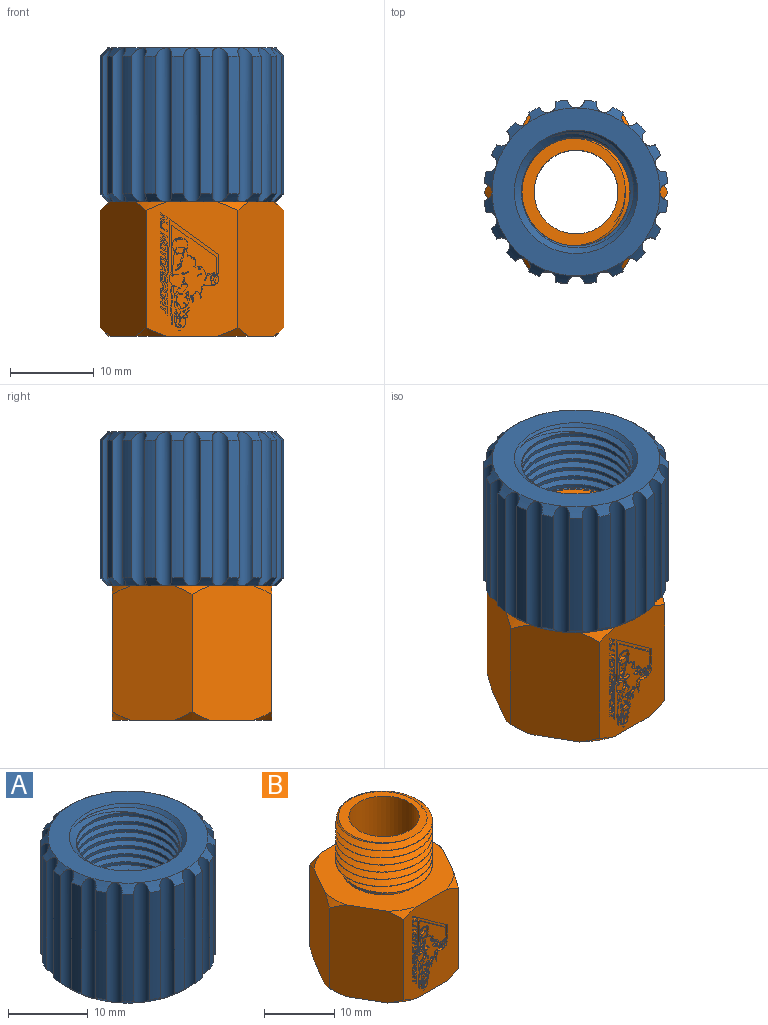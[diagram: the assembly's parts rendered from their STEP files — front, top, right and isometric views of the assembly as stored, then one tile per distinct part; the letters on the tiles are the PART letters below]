
ASSEMBLY  parts=2 mates=1
PART A: 89 faces, bbox 22x22x19 mm
  f0: cylinder r=1mm len=18.38mm, axis (0,0,1), area 53mm2, adj f35,f39,f60,f61,f80,f81
  f1: cylinder r=1mm len=18.38mm, axis (0,0,1), area 53mm2, adj f38,f39,f42,f60,f62,f80
  f2: cylinder r=1mm len=18.38mm, axis (0,0,1), area 53mm2, adj f37,f38,f42,f43,f62,f63
  f3: cylinder r=1mm len=18.38mm, axis (0,0,1), area 53mm2, adj f36,f37,f43,f44,f63,f64
  f4: cylinder r=1mm len=18.38mm, axis (0,0,1), area 53mm2, adj f34,f35,f59,f61,f79,f81
  f5: cylinder r=1mm len=18.38mm, axis (0,0,1), area 53mm2, adj f33,f34,f58,f59,f78,f79
  f6: cylinder r=1mm len=18.38mm, axis (0,0,1), area 53mm2, adj f32,f33,f57,f58,f77,f78
  f7: cylinder r=1mm len=18.38mm, axis (0,0,1), area 53mm2, adj f31,f32,f56,f57,f76,f77
  f8: cylinder r=1mm len=18.38mm, axis (0,0,1), area 53mm2, adj f30,f31,f55,f56,f75,f76
  f9: cylinder r=1mm len=18.38mm, axis (0,0,1), area 53mm2, adj f29,f30,f54,f55,f74,f75
  f10: cylinder r=1mm len=18.38mm, axis (0,0,1), area 53mm2, adj f28,f29,f53,f54,f73,f74
  f11: cylinder r=1mm len=18.38mm, axis (0,0,1), area 53mm2, adj f27,f28,f52,f53,f72,f73
  f12: cylinder r=1mm len=18.38mm, axis (0,0,1), area 53mm2, adj f26,f27,f51,f52,f71,f72
  f13: cylinder r=1mm len=18.38mm, axis (0,0,1), area 53mm2, adj f25,f26,f50,f51,f70,f71
  f14: cylinder r=1mm len=18.38mm, axis (0,0,1), area 53mm2, adj f24,f25,f49,f50,f69,f70
  f15: cylinder r=1mm len=18.38mm, axis (0,0,1), area 53mm2, adj f23,f24,f48,f49,f68,f69
  f16: cylinder r=1mm len=18.38mm, axis (0,0,1), area 53mm2, adj f22,f23,f47,f48,f67,f68
  f17: cylinder r=1mm len=18.38mm, axis (0,0,1), area 53mm2, adj f21,f22,f46,f47,f66,f67
  f18: cylinder r=1mm len=18.38mm, axis (0,0,1), area 53mm2, adj f20,f21,f45,f46,f65,f66
  f19: cylinder r=1mm len=18.38mm, axis (0,0,1), area 53mm2, adj f20,f36,f44,f45,f64,f65
  f20: cylinder r=11mm len=16.38mm, axis (0,0,-1), area 23.8mm2, adj f18,f19,f45,f65
  f21: cylinder r=11mm len=16.38mm, axis (0,0,-1), area 23.8mm2, adj f17,f18,f46,f66
  f22: cylinder r=11mm len=16.38mm, axis (0,0,-1), area 23.8mm2, adj f16,f17,f47,f67
  f23: cylinder r=11mm len=16.38mm, axis (0,0,-1), area 23.8mm2, adj f15,f16,f48,f68
  f24: cylinder r=11mm len=16.38mm, axis (0,0,-1), area 23.8mm2, adj f14,f15,f49,f69
  f25: cylinder r=11mm len=16.38mm, axis (0,0,-1), area 23.8mm2, adj f13,f14,f50,f70
  f26: cylinder r=11mm len=16.38mm, axis (0,0,-1), area 23.8mm2, adj f12,f13,f51,f71
  f27: cylinder r=11mm len=16.38mm, axis (0,0,-1), area 23.8mm2, adj f11,f12,f52,f72
  f28: cylinder r=11mm len=16.38mm, axis (0,0,-1), area 23.8mm2, adj f10,f11,f53,f73
  f29: cylinder r=11mm len=16.38mm, axis (0,0,-1), area 23.8mm2, adj f9,f10,f54,f74
  f30: cylinder r=11mm len=16.38mm, axis (0,0,-1), area 23.8mm2, adj f8,f9,f55,f75
  f31: cylinder r=11mm len=16.38mm, axis (0,0,-1), area 23.8mm2, adj f7,f8,f56,f76
  f32: cylinder r=11mm len=16.38mm, axis (0,0,-1), area 23.8mm2, adj f6,f7,f57,f77
  f33: cylinder r=11mm len=16.38mm, axis (0,0,-1), area 23.8mm2, adj f5,f6,f58,f78
  f34: cylinder r=11mm len=16.38mm, axis (0,0,-1), area 23.8mm2, adj f4,f5,f59,f79
  f35: cylinder r=11mm len=16.38mm, axis (0,0,-1), area 23.8mm2, adj f0,f4,f61,f81
  f36: cylinder r=11mm len=16.38mm, axis (0,0,-1), area 23.8mm2, adj f3,f19,f44,f64
  f37: cylinder r=11mm len=16.38mm, axis (0,0,-1), area 23.8mm2, adj f2,f3,f43,f63
  f38: cylinder r=11mm len=16.38mm, axis (0,0,-1), area 23.8mm2, adj f1,f2,f42,f62
  f39: cylinder r=11mm len=16.38mm, axis (0,0,-1), area 23.8mm2, adj f0,f1,f60,f80
  f40: plane 20x20mm, normal (0,0,1), area 144mm2, adj f62,f63,f64,f65,f66,f67,f68,f69
  f41: plane 20x20mm, normal (0,0,-1), area 137.4mm2, adj f42,f43,f44,f45,f46,f47,f48,f49
  f42: cone r=11mm half-angle=45deg, axis (0,0,1), area 2.5mm2, adj f1,f2,f38,f41
  f43: cone r=11mm half-angle=45deg, axis (0,0,1), area 2.5mm2, adj f2,f3,f37,f41
  f44: cone r=11mm half-angle=45deg, axis (0,0,1), area 2.5mm2, adj f3,f19,f36,f41
  f45: cone r=11mm half-angle=45deg, axis (0,0,1), area 2.5mm2, adj f18,f19,f20,f41
  f46: cone r=11mm half-angle=45deg, axis (0,0,1), area 2.5mm2, adj f17,f18,f21,f41
  f47: cone r=11mm half-angle=45deg, axis (0,0,1), area 2.5mm2, adj f16,f17,f22,f41
  f48: cone r=11mm half-angle=45deg, axis (0,0,1), area 2.5mm2, adj f15,f16,f23,f41
  f49: cone r=11mm half-angle=45deg, axis (0,0,1), area 2.5mm2, adj f14,f15,f24,f41
  f50: cone r=11mm half-angle=45deg, axis (0,0,1), area 2.5mm2, adj f13,f14,f25,f41
  f51: cone r=11mm half-angle=45deg, axis (0,0,1), area 2.5mm2, adj f12,f13,f26,f41
  f52: cone r=11mm half-angle=45deg, axis (0,0,1), area 2.5mm2, adj f11,f12,f27,f41
  f53: cone r=11mm half-angle=45deg, axis (0,0,1), area 2.5mm2, adj f10,f11,f28,f41
  f54: cone r=11mm half-angle=45deg, axis (0,0,1), area 2.5mm2, adj f9,f10,f29,f41
  f55: cone r=11mm half-angle=45deg, axis (0,0,1), area 2.5mm2, adj f8,f9,f30,f41
  f56: cone r=11mm half-angle=45deg, axis (0,0,1), area 2.5mm2, adj f7,f8,f31,f41
  f57: cone r=11mm half-angle=45deg, axis (0,0,1), area 2.5mm2, adj f6,f7,f32,f41
  f58: cone r=11mm half-angle=45deg, axis (0,0,1), area 2.5mm2, adj f5,f6,f33,f41
  f59: cone r=11mm half-angle=45deg, axis (0,0,1), area 2.5mm2, adj f4,f5,f34,f41
  f60: cone r=11mm half-angle=45deg, axis (0,0,1), area 2.5mm2, adj f0,f1,f39,f41
  f61: cone r=11mm half-angle=45deg, axis (0,0,1), area 2.5mm2, adj f0,f4,f35,f41
  f62: cone r=10mm half-angle=45deg, axis (0,0,-1), area 2.5mm2, adj f1,f2,f38,f40
  f63: cone r=10mm half-angle=45deg, axis (0,0,-1), area 2.5mm2, adj f2,f3,f37,f40
  f64: cone r=10mm half-angle=45deg, axis (0,0,-1), area 2.5mm2, adj f3,f19,f36,f40
  f65: cone r=10mm half-angle=45deg, axis (0,0,-1), area 2.5mm2, adj f18,f19,f20,f40
  f66: cone r=10mm half-angle=45deg, axis (0,0,-1), area 2.5mm2, adj f17,f18,f21,f40
  f67: cone r=10mm half-angle=45deg, axis (0,0,-1), area 2.5mm2, adj f16,f17,f22,f40
  f68: cone r=10mm half-angle=45deg, axis (0,0,-1), area 2.5mm2, adj f15,f16,f23,f40
  f69: cone r=10mm half-angle=45deg, axis (0,0,-1), area 2.5mm2, adj f14,f15,f24,f40
  f70: cone r=10mm half-angle=45deg, axis (0,0,-1), area 2.5mm2, adj f13,f14,f25,f40
  f71: cone r=10mm half-angle=45deg, axis (0,0,-1), area 2.5mm2, adj f12,f13,f26,f40
  f72: cone r=10mm half-angle=45deg, axis (0,0,-1), area 2.5mm2, adj f11,f12,f27,f40
  f73: cone r=10mm half-angle=45deg, axis (0,0,-1), area 2.5mm2, adj f10,f11,f28,f40
  f74: cone r=10mm half-angle=45deg, axis (0,0,-1), area 2.5mm2, adj f9,f10,f29,f40
  f75: cone r=10mm half-angle=45deg, axis (0,0,-1), area 2.5mm2, adj f8,f9,f30,f40
  f76: cone r=10mm half-angle=45deg, axis (0,0,-1), area 2.5mm2, adj f7,f8,f31,f40
  f77: cone r=10mm half-angle=45deg, axis (0,0,-1), area 2.5mm2, adj f6,f7,f32,f40
  f78: cone r=10mm half-angle=45deg, axis (0,0,-1), area 2.5mm2, adj f5,f6,f33,f40
  f79: cone r=10mm half-angle=45deg, axis (0,0,-1), area 2.5mm2, adj f4,f5,f34,f40
  f80: cone r=10mm half-angle=45deg, axis (0,0,-1), area 2.5mm2, adj f0,f1,f39,f40
  f81: cone r=10mm half-angle=45deg, axis (0,0,-1), area 2.5mm2, adj f0,f4,f35,f40
  f82: cone r=5.5mm half-angle=45deg, axis (0,0,1), area 1.1mm2, adj f83,f84,f85,f86
  f83: cone r=6.5mm half-angle=45deg, axis (0,0,-1), area 51.2mm2, adj f41,f82,f84,f85
  f84: bspline ~18.54x16.47mm, area 460.8mm2, adj f82,f83,f85,f86,f87,f88
  f85: bspline ~18.33x16.47mm, area 415.2mm2, adj f82,f83,f84,f86,f87,f88
  f86: cylinder r=6.45mm len=16.62mm, axis (0,0,-1), area 48.1mm2, adj f82,f84,f85,f87
  f87: cone r=6.5mm half-angle=45deg, axis (0,0,-1), area 1.1mm2, adj f84,f85,f86,f88
  f88: cone r=7.5mm half-angle=45deg, axis (0,0,1), area 42mm2, adj f40,f84,f85,f87
PART B: 257 faces, bbox 22.2x21.1x26.5 mm
  f0: plane 16.22x11.19mm, normal (0,-1,0), area 127.4mm2, adj f7,f8,f9,f10,f14,f16,f18,f19
  f1: cylinder r=6.9mm len=13.8mm, axis (0,0,-1), area 34.9mm2, adj f2,f3,f12,f28
  f2: bspline ~16.02x13.87mm, area 326.3mm2, adj f1,f3,f9,f11,f12,f13,f26,f28
  f3: bspline ~16.02x13.87mm, area 328.4mm2, adj f1,f2,f9,f12,f13,f26,f28
  f4: plane 16.21x9.71mm, normal (0.87,0.5,0), area 171mm2, adj f5,f8,f9,f10,f15,f17,f24,f25
  f5: plane 16.22x11.19mm, normal (0,1,0), area 171mm2, adj f4,f6,f9,f10,f22,f23,f24,f25
  f6: plane 16.21x9.71mm, normal (-0.87,0.5,0), area 171mm2, adj f5,f7,f9,f10,f20,f21,f22,f23
  f7: plane 16.21x9.71mm, normal (-0.87,-0.5,0), area 171mm2, adj f0,f6,f9,f10,f18,f19,f20,f21
  f8: plane 16.21x9.71mm, normal (0.87,-0.5,0), area 171mm2, adj f0,f4,f9,f10,f14,f15,f16,f17
  f9: plane 19.94x19mm, normal (0,0,1), area 192.7mm2, adj f0,f2,f3,f4,f5,f6,f7,f8
  f10: plane 19.94x19mm, normal (0,0,-1), area 222.3mm2, adj f0,f4,f5,f6,f7,f8,f16,f17
  f11: plane 0.01x0.01mm, normal (-0.59,-0.81,0), area 0mm2, adj f2,f9,f13
  f12: plane 12.82x12.81mm, normal (0,0,-1), area 20.6mm2, adj f1,f2,f3,f13
  f13: cylinder r=5.87mm len=11.73mm, axis (0,0,1), area 36.4mm2, adj f2,f3,f9,f11,f12
  f14: cone r=10.97mm half-angle=45deg, axis (0,0,-1), area 3.1mm2, adj f0,f8,f9
  f15: cone r=10.97mm half-angle=45deg, axis (0,0,-1), area 3.1mm2, adj f4,f8,f9
  f16: cone r=10.97mm half-angle=45deg, axis (0,0,1), area 3.1mm2, adj f0,f8,f10
  f17: cone r=10.97mm half-angle=45deg, axis (0,0,1), area 3.1mm2, adj f4,f8,f10
  f18: cone r=10.97mm half-angle=45deg, axis (0,0,-1), area 3.1mm2, adj f0,f7,f9
  f19: cone r=10.97mm half-angle=45deg, axis (0,0,1), area 3.1mm2, adj f0,f7,f10
  f20: cone r=10.97mm half-angle=45deg, axis (0,0,-1), area 3.1mm2, adj f6,f7,f9
  f21: cone r=10.97mm half-angle=45deg, axis (0,0,1), area 3.1mm2, adj f6,f7,f10
  f22: cone r=10.97mm half-angle=45deg, axis (0,0,-1), area 3.1mm2, adj f5,f6,f9
  f23: cone r=10.97mm half-angle=45deg, axis (0,0,1), area 3.1mm2, adj f5,f6,f10
  f24: cone r=10.97mm half-angle=45deg, axis (0,0,-1), area 3.1mm2, adj f4,f5,f9
  f25: cone r=10.97mm half-angle=45deg, axis (0,0,1), area 3.1mm2, adj f4,f5,f10
  f26: plane 12.82x12.37mm, normal (0,0,1), area 46.6mm2, adj f2,f3,f27,f28
  f27: cylinder r=5mm len=25.5mm, axis (0,0,1), area 801.1mm2, adj f10,f26
  f28: cone r=6.9mm half-angle=45deg, axis (0,0,-1), area 5.2mm2, adj f1,f2,f3,f26
  f29: plane 0.83x0.55mm, normal (-0.55,0,-0.83), area 0.4mm2, adj f0,f30,f38,f39
  f30: plane 0.4x0.19mm, normal (1,0,0), area 0.1mm2, adj f0,f29,f31,f39
  f31: plane 0.55x0.4mm, normal (0.55,0,0.84), area 0.3mm2, adj f0,f30,f32,f39
  f32: plane 0.55x0.4mm, normal (0.19,0,-0.98), area 0.2mm2, adj f0,f31,f33,f39
  f33: plane 0.4x0.19mm, normal (1,0,0), area 0.1mm2, adj f0,f32,f34,f39
  f34: plane 0.83x0.54mm, normal (0.55,0,0.84), area 0.4mm2, adj f0,f33,f35,f39
  f35: plane 0.4x0.18mm, normal (-1,0,0), area 0.1mm2, adj f0,f34,f36,f39
  f36: plane 0.56x0.4mm, normal (-0.55,0,-0.84), area 0.3mm2, adj f0,f35,f37,f39
  f37: plane 0.56x0.4mm, normal (-0.19,0,0.98), area 0.2mm2, adj f0,f36,f38,f39
  f38: plane 0.4x0.18mm, normal (-1,0,0), area 0.1mm2, adj f0,f29,f37,f39
  f39: plane 1.38x0.83mm, normal (0,-1,0), area 0.4mm2, adj f29,f30,f31,f32,f33,f34,f35,f36
  f40: plane 0.4x0.19mm, normal (0.54,0,0.84), area 0.1mm2, adj f41,f56,f57,f252
  f41: plane 0.46x0.4mm, normal (1,0,0), area 0.2mm2, adj f40,f42,f57,f252
  f42: plane 0.4x0.19mm, normal (-0.54,0,-0.84), area 0.1mm2, adj f41,f56,f57,f252
  f43: plane 0.83x0.54mm, normal (-0.54,0,-0.84), area 0.4mm2, adj f0,f44,f55,f57
  f44: plane 0.4x0.19mm, normal (1,0,0), area 0.1mm2, adj f0,f43,f45,f57
  f45: plane 0.4x0.27mm, normal (0.54,0,0.84), area 0.1mm2, adj f0,f44,f46,f57
  f46: plane 0.4x0.25mm, normal (1,0,0), area 0.1mm2, adj f0,f45,f47,f57
  f47: plane 0.4x0.27mm, normal (0.17,0,-0.98), area 0.1mm2, adj f0,f46,f48,f57
  f48: plane 0.4x0.18mm, normal (1,0,0), area 0.1mm2, adj f0,f47,f49,f57
  f49: plane 0.4x0.06mm, normal (0.54,0,0.84), area 0mm2, adj f0,f48,f50,f57
  f50: plane 0.4x0.22mm, normal (-0.18,0,0.98), area 0.1mm2, adj f0,f49,f51,f57
  f51: plane 0.4x0mm, normal (1,0,0), area 0mm2, adj f0,f50,f52,f57
  f52: cylinder r=0.32mm len=0.4mm, axis (0,-1,0), area 0.1mm2, adj f0,f51,f53,f57
  f53: plane 0.4x0.29mm, normal (0.54,0,0.84), area 0.1mm2, adj f0,f52,f54,f57
  f54: cylinder r=0.08mm len=0.4mm, axis (0,-1,0), area 0.1mm2, adj f0,f53,f55,f57
  f55: plane 0.69x0.4mm, normal (-1,0,0), area 0.3mm2, adj f0,f43,f54,f57
  f56: plane 0.46x0.4mm, normal (-1,0,0), area 0.2mm2, adj f40,f42,f57,f252
  f57: plane 1.31x0.83mm, normal (0,-1,0), area 0.5mm2, adj f40,f41,f42,f43,f44,f45,f46,f47
  f58: plane 0.48x0.4mm, normal (0.54,0,0.84), area 0.2mm2, adj f59,f69,f70,f253
  f59: plane 0.46x0.4mm, normal (1,0,0), area 0.2mm2, adj f58,f60,f70,f253
  f60: plane 0.48x0.4mm, normal (-0.53,0,-0.85), area 0.2mm2, adj f59,f69,f70,f253
  f61: plane 0.52x0.4mm, normal (1,0,0), area 0.2mm2, adj f0,f62,f68,f70
  f62: cylinder r=0.32mm len=0.4mm, axis (0,-1,0), area 0.1mm2, adj f0,f61,f63,f70
  f63: plane 0.56x0.4mm, normal (0.53,0,0.85), area 0.3mm2, adj f0,f62,f64,f70
  f64: cylinder r=0.08mm len=0.4mm, axis (0,-1,0), area 0.1mm2, adj f0,f63,f65,f70
  f65: plane 0.51x0.4mm, normal (-1,0,0), area 0.2mm2, adj f0,f64,f66,f70
  f66: cylinder r=0.32mm len=0.4mm, axis (0,-1,0), area 0.1mm2, adj f0,f65,f67,f70
  f67: plane 0.56x0.4mm, normal (-0.54,0,-0.84), area 0.3mm2, adj f0,f66,f68,f70
  f68: cylinder r=0.08mm len=0.4mm, axis (0,-1,0), area 0.1mm2, adj f0,f61,f67,f70
  f69: plane 0.47x0.4mm, normal (-1,0,0), area 0.2mm2, adj f58,f60,f70,f253
  f70: plane 1.23x0.83mm, normal (0,-1,0), area 0.5mm2, adj f58,f59,f60,f61,f62,f63,f64,f65
  f71: plane 0.48x0.4mm, normal (0.54,0,0.84), area 0.2mm2, adj f72,f82,f83,f254
  f72: plane 0.46x0.4mm, normal (1,0,0), area 0.2mm2, adj f71,f73,f83,f254
  f73: plane 0.48x0.4mm, normal (-0.53,0,-0.85), area 0.2mm2, adj f72,f82,f83,f254
  f74: cylinder r=0.08mm len=0.4mm, axis (0,-1,0), area 0.1mm2, adj f0,f75,f81,f83
  f75: plane 0.51x0.4mm, normal (-1,0,0), area 0.2mm2, adj f0,f74,f76,f83
  f76: cylinder r=0.32mm len=0.4mm, axis (0,-1,0), area 0.1mm2, adj f0,f75,f77,f83
  f77: plane 0.56x0.4mm, normal (-0.54,0,-0.84), area 0.3mm2, adj f0,f76,f78,f83
  f78: cylinder r=0.08mm len=0.4mm, axis (0,-1,0), area 0.1mm2, adj f0,f77,f79,f83
  f79: plane 0.52x0.4mm, normal (1,0,0), area 0.2mm2, adj f0,f78,f80,f83
  f80: cylinder r=0.32mm len=0.4mm, axis (0,-1,0), area 0.1mm2, adj f0,f79,f81,f83
  f81: plane 0.56x0.4mm, normal (0.53,0,0.85), area 0.3mm2, adj f0,f74,f80,f83
  f82: plane 0.47x0.4mm, normal (-1,0,0), area 0.2mm2, adj f71,f73,f83,f254
  f83: plane 1.23x0.83mm, normal (0,-1,0), area 0.5mm2, adj f71,f72,f73,f74,f75,f76,f77,f78
  f84: plane 0.48x0.4mm, normal (0.54,0,0.84), area 0.2mm2, adj f85,f95,f96,f255
  f85: plane 0.46x0.4mm, normal (1,0,0), area 0.2mm2, adj f84,f86,f96,f255
  f86: plane 0.48x0.4mm, normal (-0.53,0,-0.85), area 0.2mm2, adj f85,f95,f96,f255
  f87: plane 0.52x0.4mm, normal (1,0,0), area 0.2mm2, adj f0,f88,f94,f96
  f88: cylinder r=0.32mm len=0.4mm, axis (0,-1,0), area 0.1mm2, adj f0,f87,f89,f96
  f89: plane 0.56x0.4mm, normal (0.53,0,0.85), area 0.3mm2, adj f0,f88,f90,f96
  f90: cylinder r=0.08mm len=0.4mm, axis (0,-1,0), area 0.1mm2, adj f0,f89,f91,f96
  f91: plane 0.51x0.4mm, normal (-1,0,0), area 0.2mm2, adj f0,f90,f92,f96
  f92: cylinder r=0.32mm len=0.4mm, axis (0,-1,0), area 0.1mm2, adj f0,f91,f93,f96
  f93: plane 0.56x0.4mm, normal (-0.54,0,-0.84), area 0.3mm2, adj f0,f92,f94,f96
  f94: cylinder r=0.08mm len=0.4mm, axis (0,-1,0), area 0.1mm2, adj f0,f87,f93,f96
  f95: plane 0.47x0.4mm, normal (-1,0,0), area 0.2mm2, adj f84,f86,f96,f255
  f96: plane 1.23x0.83mm, normal (0,-1,0), area 0.5mm2, adj f84,f85,f86,f87,f88,f89,f90,f91
  f97: plane 0.4x0.19mm, normal (0.54,0,0.84), area 0.1mm2, adj f98,f113,f114,f256
  f98: plane 0.46x0.4mm, normal (1,0,0), area 0.2mm2, adj f97,f99,f114,f256
  f99: plane 0.4x0.19mm, normal (-0.54,0,-0.84), area 0.1mm2, adj f98,f113,f114,f256
  f100: plane 0.83x0.54mm, normal (-0.54,0,-0.84), area 0.4mm2, adj f0,f101,f112,f114
  f101: plane 0.4x0.19mm, normal (1,0,0), area 0.1mm2, adj f0,f100,f102,f114
  f102: plane 0.4x0.27mm, normal (0.54,0,0.84), area 0.1mm2, adj f0,f101,f103,f114
  f103: plane 0.4x0.25mm, normal (1,0,0), area 0.1mm2, adj f0,f102,f104,f114
  f104: plane 0.4x0.27mm, normal (0.17,0,-0.98), area 0.1mm2, adj f0,f103,f105,f114
  f105: plane 0.4x0.18mm, normal (1,0,0), area 0.1mm2, adj f0,f104,f106,f114
  f106: plane 0.4x0.06mm, normal (0.54,0,0.84), area 0mm2, adj f0,f105,f107,f114
  f107: plane 0.4x0.22mm, normal (-0.18,0,0.98), area 0.1mm2, adj f0,f106,f108,f114
  f108: plane 0.4x0mm, normal (1,0,0), area 0mm2, adj f0,f107,f109,f114
  f109: cylinder r=0.32mm len=0.4mm, axis (0,-1,0), area 0.1mm2, adj f0,f108,f110,f114
  f110: plane 0.4x0.29mm, normal (0.54,0,0.84), area 0.1mm2, adj f0,f109,f111,f114
  f111: cylinder r=0.08mm len=0.4mm, axis (0,-1,0), area 0.1mm2, adj f0,f110,f112,f114
  f112: plane 0.69x0.4mm, normal (-1,0,0), area 0.3mm2, adj f0,f100,f111,f114
  f113: plane 0.46x0.4mm, normal (-1,0,0), area 0.2mm2, adj f97,f99,f114,f256
  f114: plane 1.31x0.83mm, normal (0,-1,0), area 0.5mm2, adj f97,f98,f99,f100,f101,f102,f103,f104
  f115: cylinder r=0.32mm len=0.4mm, axis (0,-1,0), area 0.1mm2, adj f0,f116,f126,f127
  f116: plane 0.4x0.29mm, normal (0.55,0,0.83), area 0.1mm2, adj f0,f115,f117,f127
  f117: cylinder r=0.08mm len=0.4mm, axis (0,-1,0), area 0.1mm2, adj f0,f116,f118,f127
  f118: plane 0.68x0.4mm, normal (-1,0,0), area 0.3mm2, adj f0,f117,f119,f127
  f119: plane 0.83x0.55mm, normal (-0.55,0,-0.84), area 0.4mm2, adj f0,f118,f120,f127
  f120: plane 0.4x0.19mm, normal (1,0,0), area 0.1mm2, adj f0,f119,f121,f127
  f121: plane 0.4x0.27mm, normal (0.54,0,0.84), area 0.1mm2, adj f0,f120,f126,f127
  f122: plane 0.47x0.4mm, normal (-1,0,0.01), area 0.2mm2, adj f123,f125,f127,f128
  f123: plane 0.4x0.2mm, normal (0.54,0,0.84), area 0.1mm2, adj f122,f124,f127,f128
  f124: plane 0.47x0.4mm, normal (1,0,0), area 0.2mm2, adj f123,f125,f127,f128
  f125: plane 0.4x0.2mm, normal (-0.53,0,-0.85), area 0.1mm2, adj f122,f124,f127,f128
  f126: plane 0.48x0.4mm, normal (1,0,0), area 0.2mm2, adj f0,f115,f121,f127
  f127: plane 1.31x0.83mm, normal (0,-1,0), area 0.4mm2, adj f115,f116,f117,f118,f119,f120,f121,f122
  f128: plane 0.59x0.2mm, normal (0,-1,0), area 0.1mm2, adj f122,f123,f124,f125
  f129: extruded ~4.6x2.91mm, area 5.9mm2, adj f0,f130,f142,f144
  f130: extruded ~10.06x5.58mm, area 14.7mm2, adj f0,f129,f142,f144
  f131: extruded ~0.84x0.4mm, area 0.8mm2, adj f144,f221
  f132: extruded ~1.86x0.55mm, area 1.9mm2, adj f144,f222
  f133: extruded ~0.67x0.59mm, area 0.8mm2, adj f144,f223
  f134: extruded ~0.82x0.4mm, area 0.7mm2, adj f144,f224
  f135: extruded ~0.44x0.4mm, area 0.6mm2, adj f144,f225
  f136: extruded ~1x0.46mm, area 1mm2, adj f144,f226
  f137: extruded ~0.84x0.4mm, area 0.8mm2, adj f144,f227
  f138: extruded ~0.6x0.46mm, area 0.8mm2, adj f144,f228
  f139: extruded ~1.05x0.86mm, area 1.4mm2, adj f144,f229
  f140: extruded ~0.4x0.28mm, area 0.3mm2, adj f144,f230
  f141: extruded ~0.47x0.4mm, area 0.4mm2, adj f144,f231
  f142: extruded ~1.19x0.75mm, area 1.4mm2, adj f0,f129,f130,f144
  f143: extruded ~0.46x0.4mm, area 0.5mm2, adj f144,f220
  f144: plane 10.38x5.77mm, normal (0,-1,0), area 15.2mm2, adj f129,f130,f131,f132,f133,f134,f135,f136
  f145: plane 0.48x0.4mm, normal (-1,0,0), area 0.2mm2, adj f0,f146,f154,f155
  f146: plane 0.4x0.08mm, normal (0.55,0,0.83), area 0mm2, adj f0,f145,f147,f155
  f147: plane 0.4x0.17mm, normal (-1,0,0), area 0.1mm2, adj f0,f146,f148,f155
  f148: plane 0.4x0.14mm, normal (-0.55,0,-0.84), area 0.1mm2, adj f0,f147,f149,f155
  f149: cylinder r=0.08mm len=0.4mm, axis (0,-1,0), area 0.1mm2, adj f0,f148,f150,f155
  f150: plane 0.5x0.4mm, normal (1,0,0), area 0.2mm2, adj f0,f149,f151,f155
  f151: cylinder r=0.32mm len=0.4mm, axis (0,-1,0), area 0.1mm2, adj f0,f150,f152,f155
  f152: plane 0.69x0.45mm, normal (0.55,0,0.84), area 0.3mm2, adj f0,f151,f153,f155
  f153: plane 0.4x0.18mm, normal (-1,0,0), area 0.1mm2, adj f0,f152,f154,f155
  f154: plane 0.65x0.42mm, normal (-0.55,0,-0.84), area 0.3mm2, adj f0,f145,f153,f155
  f155: plane 1.3x0.83mm, normal (0,-1,0), area 0.3mm2, adj f145,f146,f147,f148,f149,f150,f151,f152
  f156: plane 0.4x0.19mm, normal (-0.54,0,-0.84), area 0.1mm2, adj f0,f157,f163,f164
  f157: plane 0.4x0.32mm, normal (1,0,0), area 0.1mm2, adj f0,f156,f158,f164
  f158: plane 0.65x0.42mm, normal (-0.54,0,-0.84), area 0.3mm2, adj f0,f157,f159,f164
  f159: plane 0.4x0.19mm, normal (1,0,0), area 0.1mm2, adj f0,f158,f160,f164
  f160: plane 0.65x0.42mm, normal (0.55,0,0.84), area 0.3mm2, adj f0,f159,f161,f164
  f161: plane 0.4x0.32mm, normal (1,0,0), area 0.1mm2, adj f0,f160,f162,f164
  f162: plane 0.4x0.19mm, normal (0.55,0,0.84), area 0.1mm2, adj f0,f161,f163,f164
  f163: plane 0.85x0.4mm, normal (-1,0,0), area 0.3mm2, adj f0,f156,f162,f164
  f164: plane 1.06x0.83mm, normal (0,-1,0), area 0.3mm2, adj f156,f157,f158,f159,f160,f161,f162,f163
  f165: plane 0.65x0.42mm, normal (0.55,0,0.84), area 0.3mm2, adj f0,f166,f172,f173
  f166: plane 0.4x0.32mm, normal (1,0,0), area 0.1mm2, adj f0,f165,f167,f173
  f167: plane 0.4x0.19mm, normal (0.55,0,0.84), area 0.1mm2, adj f0,f166,f168,f173
  f168: plane 0.85x0.4mm, normal (-1,0,0), area 0.3mm2, adj f0,f167,f169,f173
  f169: plane 0.4x0.19mm, normal (-0.54,0,-0.84), area 0.1mm2, adj f0,f168,f170,f173
  f170: plane 0.4x0.32mm, normal (1,0,0), area 0.1mm2, adj f0,f169,f171,f173
  f171: plane 0.65x0.42mm, normal (-0.54,0,-0.84), area 0.3mm2, adj f0,f170,f172,f173
  f172: plane 0.4x0.19mm, normal (1,0,0), area 0.1mm2, adj f0,f165,f171,f173
  f173: plane 1.06x0.83mm, normal (0,-1,0), area 0.3mm2, adj f165,f166,f167,f168,f169,f170,f171,f172
  f174: plane 0.46x0.4mm, normal (1,0,0), area 0.2mm2, adj f0,f175,f195,f196
  f175: plane 0.4x0.06mm, normal (-0.54,0,-0.84), area 0mm2, adj f0,f174,f176,f196
  f176: plane 0.4x0.18mm, normal (1,0,0), area 0.1mm2, adj f0,f175,f177,f196
  f177: plane 0.4x0.12mm, normal (0.54,0,0.84), area 0.1mm2, adj f0,f176,f178,f196
  f178: cylinder r=0.08mm len=0.4mm, axis (0,-1,0), area 0.1mm2, adj f0,f177,f179,f196
  f179: plane 0.51x0.4mm, normal (-1,0,0), area 0.2mm2, adj f0,f178,f180,f196
  f180: cylinder r=0.32mm len=0.4mm, axis (0,-1,0), area 0.1mm2, adj f0,f179,f181,f196
  f181: plane 0.4x0.22mm, normal (-0.53,0,-0.85), area 0.1mm2, adj f0,f180,f182,f196
  f182: cylinder r=0.08mm len=0.4mm, axis (0,-1,0), area 0.1mm2, adj f0,f181,f183,f196
  f183: plane 0.5x0.4mm, normal (1,0,0), area 0.2mm2, adj f0,f182,f184,f196
  f184: plane 0.4x0.15mm, normal (-0.53,0,-0.85), area 0.1mm2, adj f0,f183,f185,f196
  f185: plane 0.46x0.4mm, normal (-1,0,0), area 0.2mm2, adj f0,f184,f186,f196
  f186: plane 0.4x0.07mm, normal (0.53,0,0.85), area 0mm2, adj f0,f185,f187,f196
  f187: plane 0.4x0.18mm, normal (-1,0,0), area 0.1mm2, adj f0,f186,f188,f196
  f188: plane 0.4x0.13mm, normal (-0.53,0,-0.85), area 0.1mm2, adj f0,f187,f189,f196
  f189: cylinder r=0.08mm len=0.4mm, axis (0,-1,0), area 0.1mm2, adj f0,f188,f190,f196
  f190: plane 0.51x0.4mm, normal (1,0,0), area 0.2mm2, adj f0,f189,f191,f196
  f191: cylinder r=0.32mm len=0.4mm, axis (0,-1,0), area 0.1mm2, adj f0,f190,f192,f196
  f192: plane 0.4x0.23mm, normal (0.54,0,0.84), area 0.1mm2, adj f0,f191,f193,f196
  f193: cylinder r=0.08mm len=0.4mm, axis (0,-1,0), area 0.1mm2, adj f0,f192,f194,f196
  f194: plane 0.5x0.4mm, normal (-1,0,0), area 0.2mm2, adj f0,f193,f195,f196
  f195: plane 0.4x0.14mm, normal (0.54,0,0.84), area 0.1mm2, adj f0,f174,f194,f196
  f196: plane 1.23x0.83mm, normal (0,-1,0), area 0.5mm2, adj f174,f175,f176,f177,f178,f179,f180,f181
  f197: plane 6.26x0.4mm, normal (1,0,-0.01), area 2.5mm2, adj f0,f198,f205,f206
  f198: plane 0.4x0.3mm, normal (-0.47,0,0.88), area 0.1mm2, adj f0,f197,f199,f206
  f199: plane 5.54x0.4mm, normal (-1,0,0.01), area 2.2mm2, adj f0,f198,f200,f206
  f200: plane 5.33x3.82mm, normal (0.58,0,0.81), area 2.6mm2, adj f0,f199,f201,f206
  f201: plane 1.85x0.4mm, normal (1,0,0), area 0.7mm2, adj f0,f200,f202,f206
  f202: plane 0.4x0.3mm, normal (0.46,0,0.89), area 0.1mm2, adj f0,f201,f203,f206
  f203: plane 2.33x0.4mm, normal (-1,0,0), area 0.9mm2, adj f0,f202,f204,f206
  f204: plane 5.93x4.24mm, normal (-0.58,0,-0.81), area 2.9mm2, adj f0,f203,f205,f206
  f205: plane 0.4x0.18mm, normal (1,0,0), area 0.1mm2, adj f0,f197,f204,f206
  f206: plane 6.57x5.98mm, normal (0,-1,0), area 5.4mm2, adj f197,f198,f199,f200,f201,f202,f203,f204
  f207: plane 0.83x0.55mm, normal (-0.55,0,-0.84), area 0.4mm2, adj f0,f208,f218,f219
  f208: plane 0.4x0.18mm, normal (1,0,0), area 0.1mm2, adj f0,f207,f209,f219
  f209: plane 0.55x0.4mm, normal (0.54,0,0.84), area 0.3mm2, adj f0,f208,f210,f219
  f210: plane 0.4x0.33mm, normal (0.23,0,-0.97), area 0.1mm2, adj f0,f209,f211,f219
  f211: plane 0.49x0.4mm, normal (0.84,0,0.55), area 0.2mm2, adj f0,f210,f212,f219
  f212: plane 0.54x0.4mm, normal (-0.55,0,-0.84), area 0.3mm2, adj f0,f211,f213,f219
  f213: plane 0.4x0.19mm, normal (1,0,0), area 0.1mm2, adj f0,f212,f214,f219
  f214: plane 0.83x0.54mm, normal (0.54,0,0.84), area 0.4mm2, adj f0,f213,f215,f219
  f215: plane 0.4x0.2mm, normal (-1,0,0), area 0.1mm2, adj f0,f214,f216,f219
  f216: plane 0.49x0.4mm, normal (-0.83,0,-0.56), area 0.2mm2, adj f0,f215,f217,f219
  f217: plane 0.4x0.34mm, normal (-0.15,0,0.99), area 0.1mm2, adj f0,f216,f218,f219
  f218: plane 0.4x0.19mm, normal (-1,0,0), area 0.1mm2, adj f0,f207,f217,f219
  f219: plane 1.48x0.83mm, normal (0,-1,0), area 0.5mm2, adj f207,f208,f209,f210,f211,f212,f213,f214
  f220: plane 0.47x0.32mm, normal (0,-1,0), area 0mm2, adj f143
  f221: plane 0.85x0.28mm, normal (0,-1,0), area 0.1mm2, adj f131
  f222: plane 1.88x0.56mm, normal (0,-1,0), area 0.2mm2, adj f132
  f223: plane 0.68x0.6mm, normal (0,-1,0), area 0.1mm2, adj f133
  f224: plane 0.83x0.34mm, normal (0,-1,0), area 0.1mm2, adj f134
  f225: plane 0.45x0.31mm, normal (0,-1,0), area 0mm2, adj f135
  f226: plane 1.01x0.49mm, normal (0,-1,0), area 0.2mm2, adj f136
  f227: plane 0.84x0.28mm, normal (0,-1,0), area 0.1mm2, adj f137
  f228: plane 0.61x0.46mm, normal (0,-1,0), area 0.1mm2, adj f138
  f229: plane 1.06x0.87mm, normal (0,-1,0), area 0.6mm2, adj f139
  f230: plane 0.28x0.28mm, normal (0,-1,0), area 0.1mm2, adj f140
  f231: plane 0.48x0.25mm, normal (0,-1,0), area 0mm2, adj f141
  f232: extruded ~0.4x0.36mm, area 0.4mm2, adj f0,f233
  f233: plane 0.36x0.3mm, normal (0,-1,0), area 0mm2, adj f232
  f234: extruded ~1.65x0.69mm, area 1.7mm2, adj f0,f235
  f235: plane 1.68x0.71mm, normal (0,-1,0), area 0.5mm2, adj f234
  f236: extruded ~1.71x0.73mm, area 2.5mm2, adj f0,f237
  f237: plane 1.77x0.76mm, normal (0,-1,0), area 0.4mm2, adj f236
  f238: extruded ~0.4x0.16mm, area 0.2mm2, adj f0,f239
  f239: plane 0.17x0.1mm, normal (0,-1,0), area 0mm2, adj f238
  f240: extruded ~0.82x0.55mm, area 0.8mm2, adj f0,f241
  f241: plane 0.83x0.55mm, normal (0,-1,0), area 0.1mm2, adj f240
  f242: extruded ~0.58x0.4mm, area 0.5mm2, adj f0,f243
  f243: plane 0.59x0.16mm, normal (0,-1,0), area 0mm2, adj f242
  f244: extruded ~0.82x0.53mm, area 0.9mm2, adj f0,f245
  f245: plane 0.84x0.55mm, normal (0,-1,0), area 0.3mm2, adj f244
  f246: extruded ~0.4x0.21mm, area 0.2mm2, adj f0,f247
  f247: plane 0.22x0.07mm, normal (0,-1,0), area 0mm2, adj f246
  f248: extruded ~0.44x0.4mm, area 0.4mm2, adj f0,f249
  f249: plane 0.47x0.24mm, normal (0,-1,0), area 0.1mm2, adj f248
  f250: extruded ~1.59x1.01mm, area 2.4mm2, adj f0,f251
  f251: plane 1.63x1.02mm, normal (0,-1,0), area 0.8mm2, adj f250
  f252: plane 0.59x0.19mm, normal (0,-1,0), area 0.1mm2, adj f40,f41,f42,f56
  f253: plane 0.77x0.48mm, normal (0,-1,0), area 0.2mm2, adj f58,f59,f60,f69
  f254: plane 0.77x0.48mm, normal (0,-1,0), area 0.2mm2, adj f71,f72,f73,f82
  f255: plane 0.77x0.48mm, normal (0,-1,0), area 0.2mm2, adj f84,f85,f86,f95
  f256: plane 0.59x0.19mm, normal (0,-1,0), area 0.1mm2, adj f97,f98,f99,f113
PLACE A t=(-9.36,2.83,13.98)mm
PLACE B t=(-9.36,2.83,-0.54)mm
MATE slider A.f82 <-> B.f1  axis (0,0,-1) through (-9.36,2.83,15.46)mm
